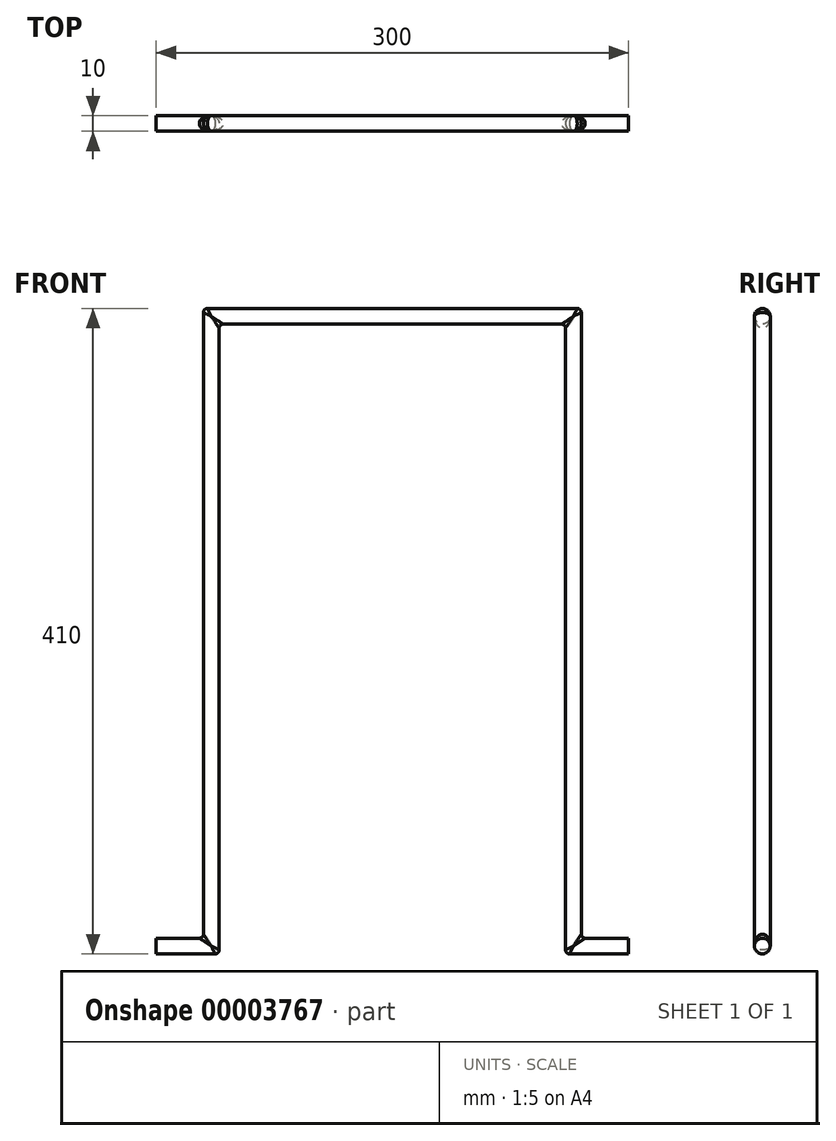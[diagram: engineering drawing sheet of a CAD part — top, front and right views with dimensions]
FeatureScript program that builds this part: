
annotation { "Feature Type Name" : "Feature", "Feature Type Description" : "" }
export const myFeature = defineFeature(function(context is Context, id is Id, definition is map)
    precondition{}
    {
        {
            var Q0;
            Q0=qCreatedBy(makeId("Front.planeOp"),FACE);
            var sketch = newSketch(context, id + "F0", { "sketchPlane" : qUnion([Q0])});
            skLineSegment(sketch, "E0.rect.bottom", {"start": v(-115, 200) * mm, "end": v(115, 200) * mm});
            skLineSegment(sketch, "E0.rect.left", {"start": v(-115, 200) * mm, "end": v(-115, -200) * mm});
            skLineSegment(sketch, "E0.rect.right", {"start": v(115, 200) * mm, "end": v(115, -200) * mm});
            skPoint(sketch, "E0.rect.middle", {"position": v(0, 0) * mm});
            skLineSegment(sketch, "E1", {"start": v(-115, -200) * mm, "end": v(-150, -200) * mm});
            skLineSegment(sketch, "E2", {"start": v(115, -200) * mm, "end": v(150, -200) * mm});
            skSolve(sketch);
        }
        {
            var Q0;
            Q0=qCreatedBy(makeId("Right.planeOp"),FACE);
            cPlane(context, id + "F1", {"entities" : qUnion([Q0]), "cplaneType" : CPlaneType.OFFSET, "offset" : 150 * mm, "oppositeDirection" : true, "width" : 152.4 * mm, "height" : 152.4 * mm});
        }
        {
            var Q0;
            Q0=qCreatedBy(id+"F1.planeOp",FACE);
            var sketch = newSketch(context, id + "F2", { "sketchPlane" : qUnion([Q0])});
            skCircle(sketch, "E3", {"center": v(0, -200) * mm, "radius": 5 * mm});
            skSolve(sketch);
        }
        {
            var Q0;
            Q0=makeQuery(id+"F2.imprint","IMPRINT",FACE,{"disambiguationData":[TD([[makeQuery(id+"F2.imprint","IMPRINT",EDGE,{"derivedFrom":sQuery(id+"F2.wireOp",EDGE,"E3")}),1.0]])]});
            var Q1;
            Q1=sQuery(id+"F0.wireOp",EDGE,"E1");
            var Q2;
            Q2=sQuery(id+"F0.wireOp",EDGE,"E0.rect.left");
            var Q3;
            Q3=sQuery(id+"F0.wireOp",EDGE,"E0.rect.bottom");
            var Q4;
            Q4=sQuery(id+"F0.wireOp",EDGE,"E0.rect.right");
            var Q5;
            Q5=sQuery(id+"F0.wireOp",EDGE,"E2");
            sweep(context, id + "F3", {"profiles" : qUnion([Q0]), "path" : qUnion([Q1, Q2, Q3, Q4, Q5])});
        }
        {
            var Q0;
            Q0=makeQuery(id+"F3.opSweep","MID_CAP_EDGE",EDGE,{"disambiguationData":[OSD([sQuery(id+"F0.wireOp",VERTEX,"E0.rect.bottom.start"),sQuery(id+"F2.wireOp",EDGE,"E3")])],"capPos":2.0});
            var Q1;
            Q1=makeQuery(id+"F3.opSweep","MID_CAP_EDGE",EDGE,{"disambiguationData":[OSD([sQuery(id+"F0.wireOp",VERTEX,"E0.rect.right.start"),sQuery(id+"F2.wireOp",EDGE,"E3")])],"capPos":3.0});
            var Q2;
            Q2=makeQuery(id+"F3.opSweep","MID_CAP_EDGE",EDGE,{"disambiguationData":[OSD([sQuery(id+"F0.wireOp",VERTEX,"E0.rect.left.end"),sQuery(id+"F2.wireOp",EDGE,"E3")])],"capPos":1.0});
            var Q3;
            Q3=makeQuery(id+"F3.opSweep","MID_CAP_EDGE",EDGE,{"disambiguationData":[OSD([sQuery(id+"F0.wireOp",VERTEX,"E2.start"),sQuery(id+"F2.wireOp",EDGE,"E3")])],"capPos":4.0});
            fillet(context, id + "F4", {"entities" : qUnion([Q0, Q1, Q2, Q3]), "radius" : 2.54 * mm, "tangentPropagation" : true, "allowEdgeOverflow" : false});
        }
    });
